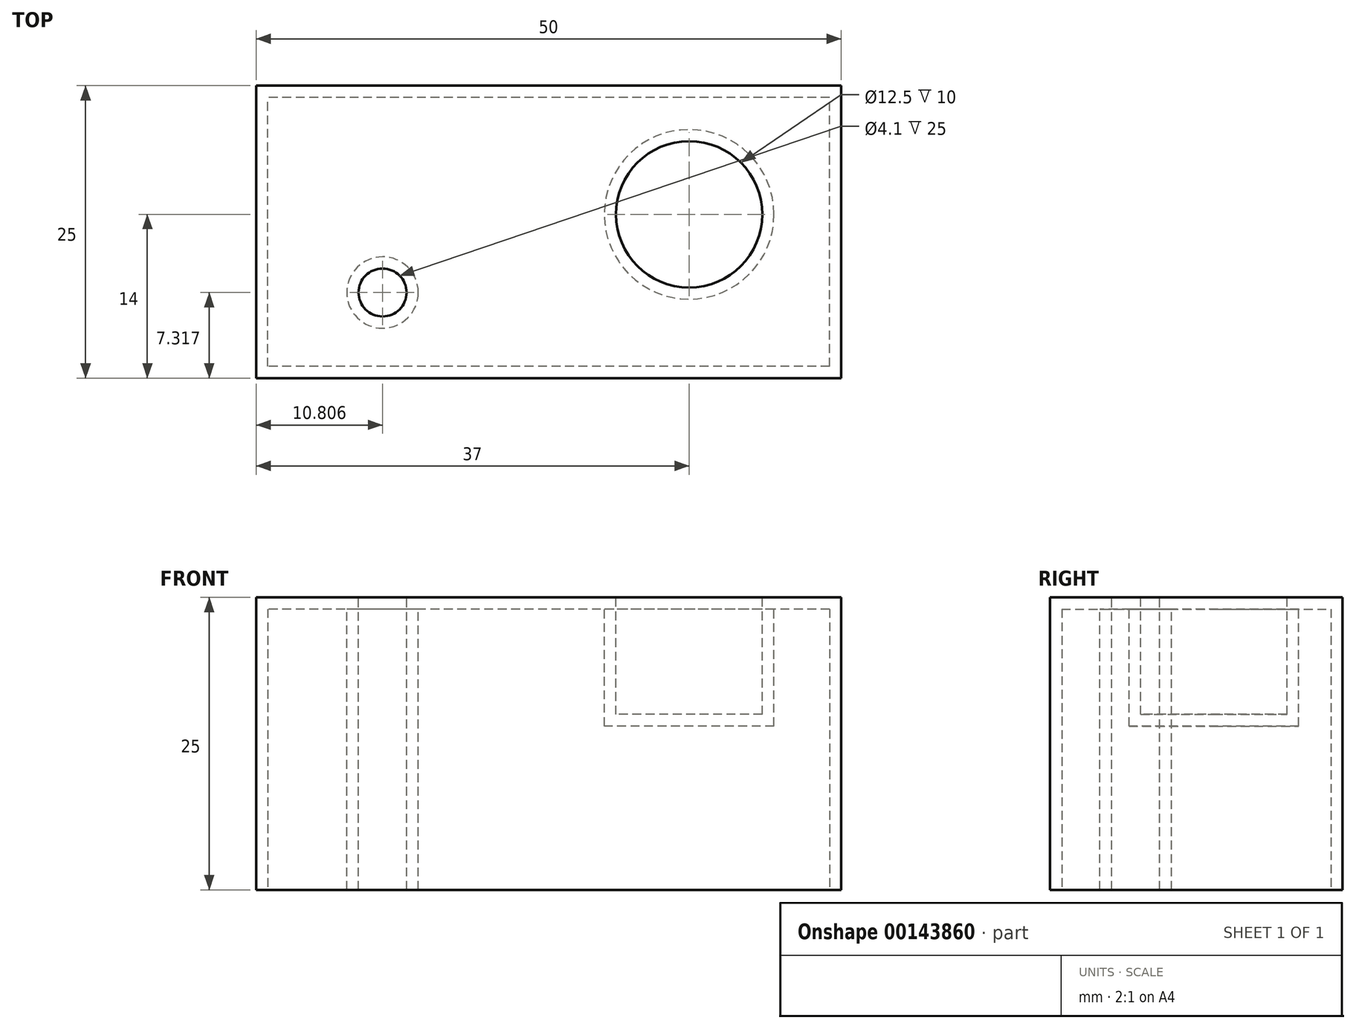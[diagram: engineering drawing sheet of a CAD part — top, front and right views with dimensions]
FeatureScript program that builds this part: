
annotation { "Feature Type Name" : "Feature", "Feature Type Description" : "" }
export const myFeature = defineFeature(function(context is Context, id is Id, definition is map)
    precondition{}
    {
        {
            var Q0;
            Q0=qCreatedBy(makeId("Top.planeOp"),FACE);
            var sketch = newSketch(context, id + "F0", { "sketchPlane" : qUnion([Q0])});
            skLineSegment(sketch, "E0.bottom", {"start": v(25, -12.5) * mm, "end": v(-25, -12.5) * mm});
            skLineSegment(sketch, "E0.top", {"start": v(25, 12.5) * mm, "end": v(-25, 12.5) * mm});
            skLineSegment(sketch, "E0.left", {"start": v(25, -12.5) * mm, "end": v(25, 12.5) * mm});
            skLineSegment(sketch, "E0.right", {"start": v(-25, -12.5) * mm, "end": v(-25, 12.5) * mm});
            skPoint(sketch, "E0.middle", {"position": v(0, 0) * mm});
            skSolve(sketch);
        }
        {
            var Q0;
            Q0 = qSketchRegion(id + "F0", true);
            extrude(context, id + "F1", {"entities" : qUnion([Q0]), "depth" : 25 * mm});
        }
        {
            var Q0;
            Q0=makeQuery(id+"F1.opExtrude","CAP_FACE",FACE,{"disambiguationData":[OSD([sQuery(id+"F0.wireOp",EDGE,"E0.bottom"),sQuery(id+"F0.wireOp",EDGE,"E0.top"),sQuery(id+"F0.wireOp",EDGE,"E0.left"),sQuery(id+"F0.wireOp",EDGE,"E0.right")])],"isStart":false});
            var sketch = newSketch(context, id + "F2", { "sketchPlane" : qUnion([Q0])});
            skCircle(sketch, "E1", {"center": v(12, 1.5) * mm, "radius": 6.25 * mm});
            skSolve(sketch);
        }
        {
            var Q0;
            Q0 = qSketchRegion(id + "F2", true);
            extrude(context, id + "F3", {"entities" : qUnion([Q0]), "operationType" : NewBodyOperationType.REMOVE, "oppositeDirection" : true, "depth" : 10 * mm});
        }
        {
            var Q0;
            Q0=makeQuery(id+"F1.opExtrude","CAP_FACE",FACE,{"disambiguationData":[OSD([sQuery(id+"F0.wireOp",EDGE,"E0.bottom"),sQuery(id+"F0.wireOp",EDGE,"E0.top"),sQuery(id+"F0.wireOp",EDGE,"E0.left"),sQuery(id+"F0.wireOp",EDGE,"E0.right")])],"isStart":false});
            var sketch = newSketch(context, id + "F4", { "sketchPlane" : qUnion([Q0])});
            skPoint(sketch, "E2", {"position": v(-14.2, -5.18) * mm});
            skSolve(sketch);
        }
        {
            var Q0;
            Q0=sQuery(id+"F4.wireOp",VERTEX,"E2");
            var Q1;
            Q1=makeQuery(id+"F1.opExtrude","SWEPT_BODY",BODY,{"disambiguationData":[OSD([sQuery(id+"F0.wireOp",EDGE,"E0.bottom"),sQuery(id+"F0.wireOp",EDGE,"E0.top"),sQuery(id+"F0.wireOp",EDGE,"E0.left"),sQuery(id+"F0.wireOp",EDGE,"E0.right")])]});
            hole(context, id + "F5", {"style" : HoleStyle.SIMPLE, "endStyle" : HoleEndStyle.THROUGH, "standardTappedOrClearance" : lookupTablePath({ "standard" : "ISO", "engagement" : "75%", "pitch" : "0.9 mm", "size" : "M5", "type" : "Tapped" }), "standardBlindInLast" : lookupTablePath({ "standard" : "ISO", "engagement" : "75%", "pitch" : "0.9 mm", "size" : "M5", "type" : "Tapped" }), "holeDiameter" : 4.1 * mm, "locations" : qUnion([Q0]), "scope" : qUnion([Q1]), "isTappedThrough" : true, "showTappedDepth" : true});
        }
        {
            var Q0;
            Q0=makeQuery(id+"F1.opExtrude","CAP_FACE",FACE,{"disambiguationData":[OSD([sQuery(id+"F0.wireOp",EDGE,"E0.bottom"),sQuery(id+"F0.wireOp",EDGE,"E0.top"),sQuery(id+"F0.wireOp",EDGE,"E0.left"),sQuery(id+"F0.wireOp",EDGE,"E0.right")])],"isStart":true});
            shell(context, id + "F6", {"entities" : qUnion([Q0]), "thickness" : 1 * mm});
        }
    });
